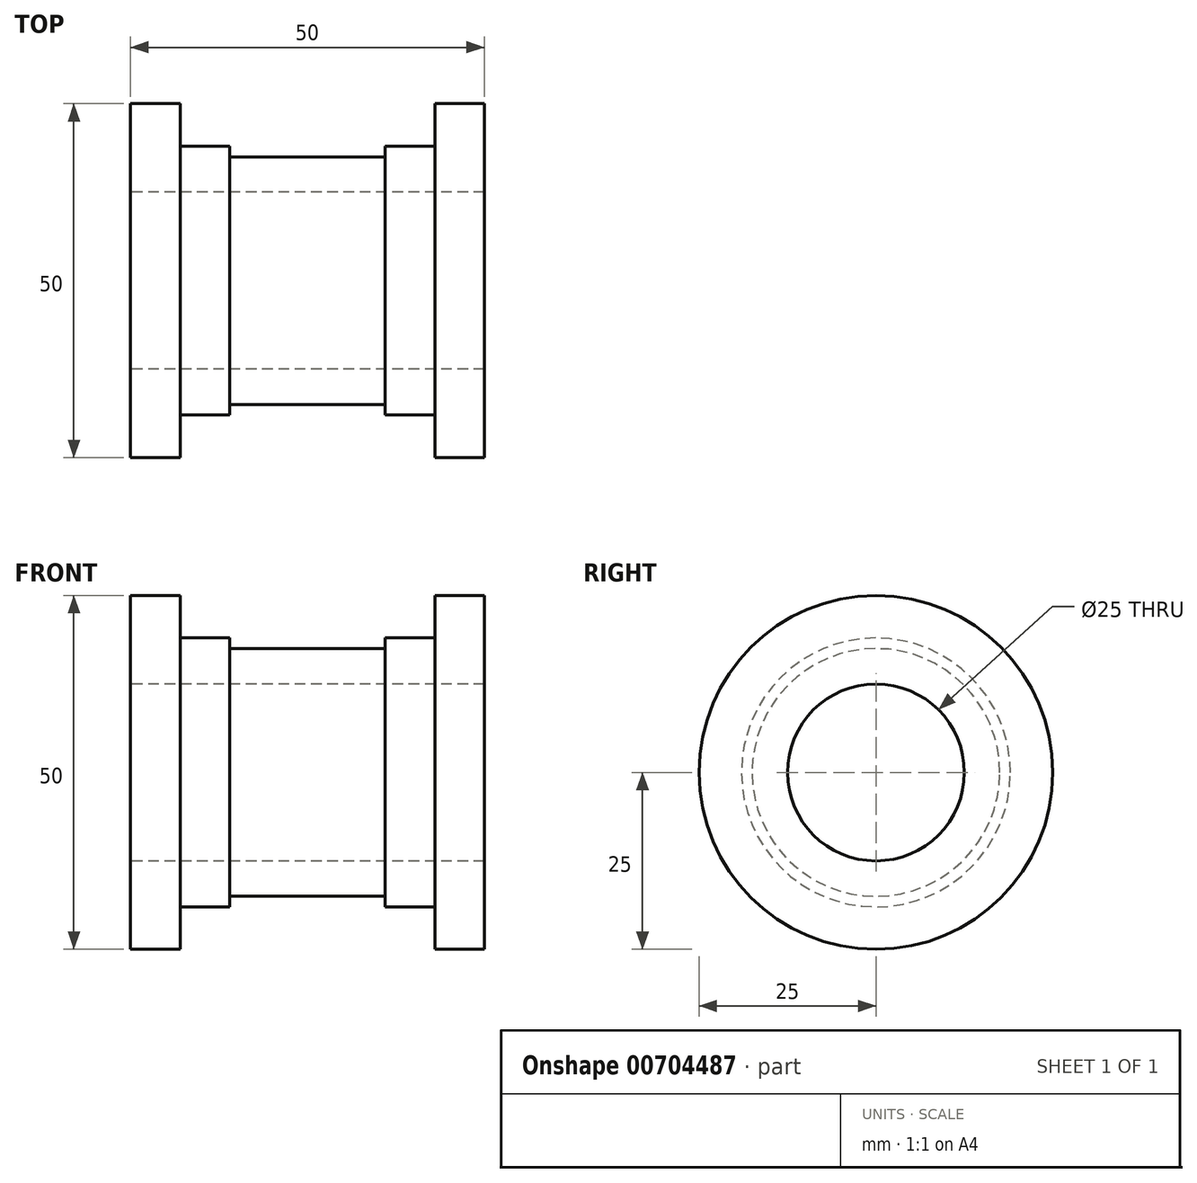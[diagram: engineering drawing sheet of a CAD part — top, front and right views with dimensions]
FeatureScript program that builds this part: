
annotation { "Feature Type Name" : "Feature", "Feature Type Description" : "" }
export const myFeature = defineFeature(function(context is Context, id is Id, definition is map)
    precondition{}
    {
        {
            var Q0;
            Q0=qCreatedBy(makeId("Front.planeOp"),FACE);
            var sketch = newSketch(context, id + "F0", { "sketchPlane" : qUnion([Q0])});
            skLineSegment(sketch, "E0", {"start": v(0, 0) * mm, "end": v(60, 0) * mm, "construction": true});
            skLineSegment(sketch, "E1", {"start": v(0, 12.5) * mm, "end": v(0, 25) * mm});
            skLineSegment(sketch, "E2", {"start": v(0, 25) * mm, "end": v(7, 25) * mm});
            skLineSegment(sketch, "E3", {"start": v(7, 25) * mm, "end": v(7, 19) * mm});
            skLineSegment(sketch, "E4", {"start": v(7, 19) * mm, "end": v(14, 19) * mm});
            skLineSegment(sketch, "E5", {"start": v(14, 19) * mm, "end": v(14, 17.5) * mm});
            skLineSegment(sketch, "E6", {"start": v(14, 17.5) * mm, "end": v(36, 17.5) * mm});
            skLineSegment(sketch, "E7", {"start": v(36, 17.5) * mm, "end": v(36, 19) * mm});
            skLineSegment(sketch, "E8", {"start": v(36, 19) * mm, "end": v(43, 19) * mm});
            skLineSegment(sketch, "E9", {"start": v(43, 19) * mm, "end": v(43, 25) * mm});
            skLineSegment(sketch, "E10", {"start": v(43, 25) * mm, "end": v(50, 25) * mm});
            skLineSegment(sketch, "E11", {"start": v(50, 25) * mm, "end": v(50, 12.5) * mm});
            skLineSegment(sketch, "E12", {"start": v(50, 12.5) * mm, "end": v(0, 12.5) * mm});
            skPoint(sketch, "E13.orphan", {"position": v(55.26, 12.5) * mm});
            skSolve(sketch);
        }
        {
            var Q0;
            Q0=qSketchRegion(id+"F0",true);
            var Q1;
            Q1=sQuery(id+"F0.wireOp",EDGE,"E0");
            revolve(context, id + "F1", {"entities" : qUnion([Q0]), "axis" : qUnion([Q1]), "revolveType" : RevolveType.FULL});
        }
    });
